# Revit family: 0042217
name_source: partatom
category: Lighting Fixtures
revit_build: Autodesk Revit 2017 (Build: 20190507_1515(x64)
units: mm (PartAtom-declared; Revit-internal decimal feet)

## family parameters
Cut with Voids When Loaded = No
Host = Face
Light Source = Yes
OmniClass Number = 23.80.70.00
OmniClass Title = Lighting
Part Type = Normal
Room Calculation Point = No
Round Connector Dimension = Use Diameter
Shared = No

## types (15) — shared parameters
-LUMDEPTH_SYL = -277 mm
Assembly Code = D5020200
AssetType = Fixed
BOX_WIDTH_SYL = 40 mm  [stored 0.131234 ft]
ClassificationName = Uniclass2015
ClassificationValue = EF_70_80
Color Filter = 16777215
DEPTH_SYL = 298 mm
Default Elevation = 1219 mm
Dimming Lamp Color Temperature Shift = <None>
DocumentationLiterature = http://www.sylvania-lighting.com
ElectricShockClassification = Class II
Emit Shape Visible in Rendering = No
Emit from Circle Diameter = 610 mm
HEIGHTBOTT_SYL = 7 mm  [stored 0.0229659 ft]
HEIGHT_SYL = 33 mm  [stored 0.108268 ft]
IfcExportAs = IfcLightFixtureType
IfcExportType = IfcLightFixtureType
ImpactProtectionIndex = IK03
IngressProtection = IP40/20
Keynote = 16500
LUMDEPTH_SYL = 277 mm
LUMWIDTH_SYL = 277 mm
Lamp = LED
LampColourRenderingIndex = 80
LampsType = LED
MAINHEIGHT_SYL = 63 mm
Manufacturer = Feilo Sylvania
ManufacturerName = Feilo Sylvania
Material = aluminium,steel housing, other diffuser
Material_1_SYL = <By Category>
Material_2_SYL = <By Category>
Material_3_SYL = <By Category>
Material_4_SYL = <By Category>
NominalDepth = 595 mm
NominalLength = 595 mm
PowerFactor = 0.9
TOPWIDTH_SYL = 245 mm  [stored 0.803806 ft]
Tilt Angle = -90.00°
Type Image = <None>
URL = http://www.sylvania-lighting.com
Voltage = 0 V
WIDTH_SYL = 298 mm
zero-valued in all types: Cost

## per-type parameters (varying)
| type | Apparent Load | LampColourTemperature | LampMacAdamStep | LampNominalLuminous | LuminousEfficacy | Model | ModelNumber | ModelReference | Name | NominalHeight | Photometric Web File | PowerConsumption | TypeName |
| 0042247 ST PANEL 600X600 HE DALI 4300LM 840 | 34 VA | 4000 K | 3 | 4300 lm | 126 lm/W | START Panel 600x600 HE DALI 4300Lm 840 | 0042247 | START Panel 600x600 HE DALI 4300Lm 840 | START Panel 600x600 HE DALI 4300Lm 840 | 34 mm | 0042247.ies | 34 W | START Panel 600x600 HE DALI 4300Lm 840 |
| 0042246 ST PANEL 600X600 HE DALI 4100LM 830 | 34 VA | 3000 K | 3 | 4100 lm | 121 lm/W | START Panel 600x600 HE DALI 4100Lm 830 | 0042246 | START Panel 600x600 HE DALI 4100Lm 830 | START Panel 600x600 HE DALI 4100Lm 830 | 34 mm | 0042246.ies | 34 W | START Panel 600x600 HE DALI 4100Lm 830 |
| 0042245 ST PANEL 600X600 DALI 4000LM 865 | 36 VA | 6500 K | 6 | 4000 lm | 111 lm/W | START Panel 600x600 DALI 4000Lm 865 | 0042245 | START Panel 600x600 DALI 4000Lm 865 | START Panel 600x600 DALI 4000Lm 865 | 34 mm | 0042245.ies | 36 W | START Panel 600x600 DALI 4000Lm 865 |
| 0042244 ST PANEL 600X600 DALI 4000LM 840 | 36 VA | 4000 K | 3 | 4000 lm | 111 lm/W | START Panel 600x600 DALI 4000Lm 840 | 0042244 | START Panel 600x600 DALI 4000Lm 840 | START Panel 600x600 DALI 4000Lm 840 | 34 mm | 0042244.ies | 36 W | START Panel 600x600 DALI 4000Lm 840 |
| 0042243 ST PANEL 600X600 DALI 3800LM 830 | 36 VA | 3000 K | 3 | 3800 lm | 106 lm/W | START Panel 600x600 DALI 3800Lm 830 | 0042243 | START Panel 600x600 DALI 3800Lm 830 | START Panel 600x600 DALI 3800Lm 830 | 34 mm | 0042243.ies | 36 W | START Panel 600x600 DALI 3800Lm 830 |
| 0042218 ST PANEL UGR19 600X600 DALI 4800LM 865 | 43 VA | 6500 K | 6 | 4800 lm | 112 lm/W | START Panel UGR19 600x600 DALI 4800Lm 865 | 0042218 | START Panel UGR19 600x600 DALI 4800Lm 865 | START Panel UGR19 600x600 DALI 4800Lm 865 | 34 mm | 0042218.ies | 43 W | START Panel UGR19 600x600 DALI 4800Lm 865 |
| 0042217 ST PANEL UGR19 600X600 DALI 4800LM 840 | 43 VA | 4000 K | 3 | 4800 lm | 112 lm/W | START Panel UGR19 600x600 DALI 4800Lm 840 | 0042217 | START Panel UGR19 600x600 DALI 4800Lm 840 | START Panel UGR19 600x600 DALI 4800Lm 840 | 34 mm | 0042217.ies | 43 W | START Panel UGR19 600x600 DALI 4800Lm 840 |
| 0042216 ST PANEL UGR19 600X600 DALI 4600LM 830 | 43 VA | 3000 K | 3 | 4600 lm | 107 lm/W | START Panel UGR19 600x600 DALI 4600Lm 830 | 0042216 | START Panel UGR19 600x600 DALI 4600Lm 830 | START Panel UGR19 600x600 DALI 4600Lm 830 | 34 mm | 0042216.ies | 43 W | START Panel UGR19 600x600 DALI 4600Lm 830 |
| 0042215 ST PANEL UGR19 600X600 DALI 4000LM 865 | 36 VA | 6500 K | 6 | 4000 lm | 111 lm/W | START Panel UGR19 600x600 DALI 4000Lm 865 | 0042215 | START Panel UGR19 600x600 DALI 4000Lm 865 | START Panel UGR19 600x600 DALI 4000Lm 865 | 35 mm | 0042215.ies | 36 W | START Panel UGR19 600x600 DALI 4000Lm 865 |
| 0042214 ST PANEL UGR19 600X600 DALI 4000LM 840 | 36 VA | 4000 K | 3 | 4000 lm | 111 lm/W | START Panel UGR19 600x600 DALI 4000Lm 840 | 0042214 | START Panel UGR19 600x600 DALI 4000Lm 840 | START Panel UGR19 600x600 DALI 4000Lm 840 | 35 mm | 0042214.ies | 36 W | START Panel UGR19 600x600 DALI 4000Lm 840 |
| 0042213 ST PANEL UGR19 600X600 DALI 3800LM 830 | 36 VA | 3000 K | 3 | 3800 lm | 106 lm/W | START Panel UGR19 600x600 DALI 3800Lm 830 | 0042213 | START Panel UGR19 600x600 DALI 3800Lm 830 | START Panel UGR19 600x600 DALI 3800Lm 830 | 35 mm | 0042213.ies | 36 W | START Panel UGR19 600x600 DALI 3800Lm 830 |
| 0042212 ST PANEL UGR19 600X600 DALI 3600LM 865 | 36 VA | 6500 K | 6 | 3600 lm | 100 lm/W | START Panel UGR19 600x600 DALI 3600Lm 865 | 0042212 | START Panel UGR19 600x600 DALI 3600Lm 865 | START Panel UGR19 600x600 DALI 3600Lm 865 | 35 mm | 0042212.ies | 36 W | START Panel UGR19 600x600 DALI 3600Lm 865 |
| 0042211 ST PANEL UGR19 600X600 DALI 3600LM 840 | 36 VA | 4000 K | 3 | 3600 lm | 100 lm/W | START Panel UGR19 600x600 DALI 3600Lm 840 | 0042211 | START Panel UGR19 600x600 DALI 3600Lm 840 | START Panel UGR19 600x600 DALI 3600Lm 840 | 35 mm | 0042211.ies | 36 W | START Panel UGR19 600x600 DALI 3600Lm 840 |
| 0042210 ST PANEL UGR19 600X600 DALI 3400LM 830 | 36 VA | 3000 K | 3 | 3400 lm | 94 lm/W | START Panel UGR19 600x600 DALI 3400Lm 830 | 0042210 | START Panel UGR19 600x600 DALI 3400Lm 830 | START Panel UGR19 600x600 DALI 3400Lm 830 | 35 mm | 0042210.ies | 36 W | START Panel UGR19 600x600 DALI 3400Lm 830 |
| 0042248 ST PANEL 600X600 HE DALI 4300LM 865 | 34 VA | 6500 K | 6 | 4300 lm | 126 lm/W | START Panel 600x600 HE DALI 4300Lm 865 | 0042248 | START Panel 600x600 HE DALI 4300Lm 865 | START Panel 600x600 HE DALI 4300Lm 865 | 34 mm | 0042248.ies | 34 W | START Panel 600x600 HE DALI 4300Lm 865 |

note: [stored X ft] marks values corroborated as IEEE doubles in the binary element streams (Revit-internal decimal feet)

## geometry (parser evidence)
native form markers: Sweep x3
no freeform markers — native parametric forms only
